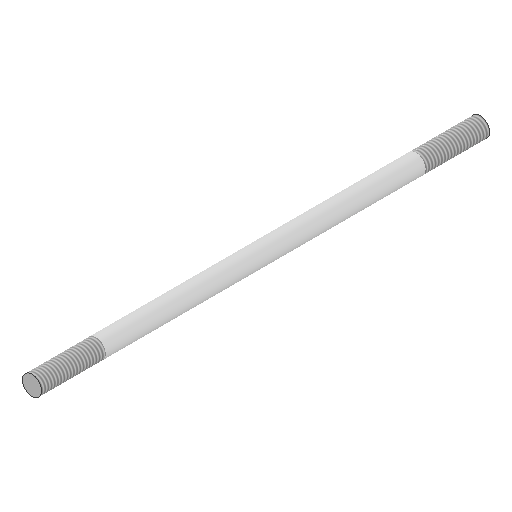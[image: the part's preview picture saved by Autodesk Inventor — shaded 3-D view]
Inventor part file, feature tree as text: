
AUTODESK INVENTOR PART (.ipt)
format: ipt  version: 2025.1 (Build 291241000, 241)  size: 104,448 bytes
history: native  units: mm
features: thread x2, other x1, extrude x1, sketch x1
ambient origin geometry x8: Origin, YZ Plane, XZ Plane, XY Plane, X Axis, Y Axis, Z Axis, Center Point
bodies: Body1 (feature_tree)
feature tree (5):
  other  "Bryła1"
  extrude  "Wyciągnięcie proste1"  Depth=3.0mm
  thread  "Gwint3"
  thread  "Gwint4"
  sketch  "Szkic1"
